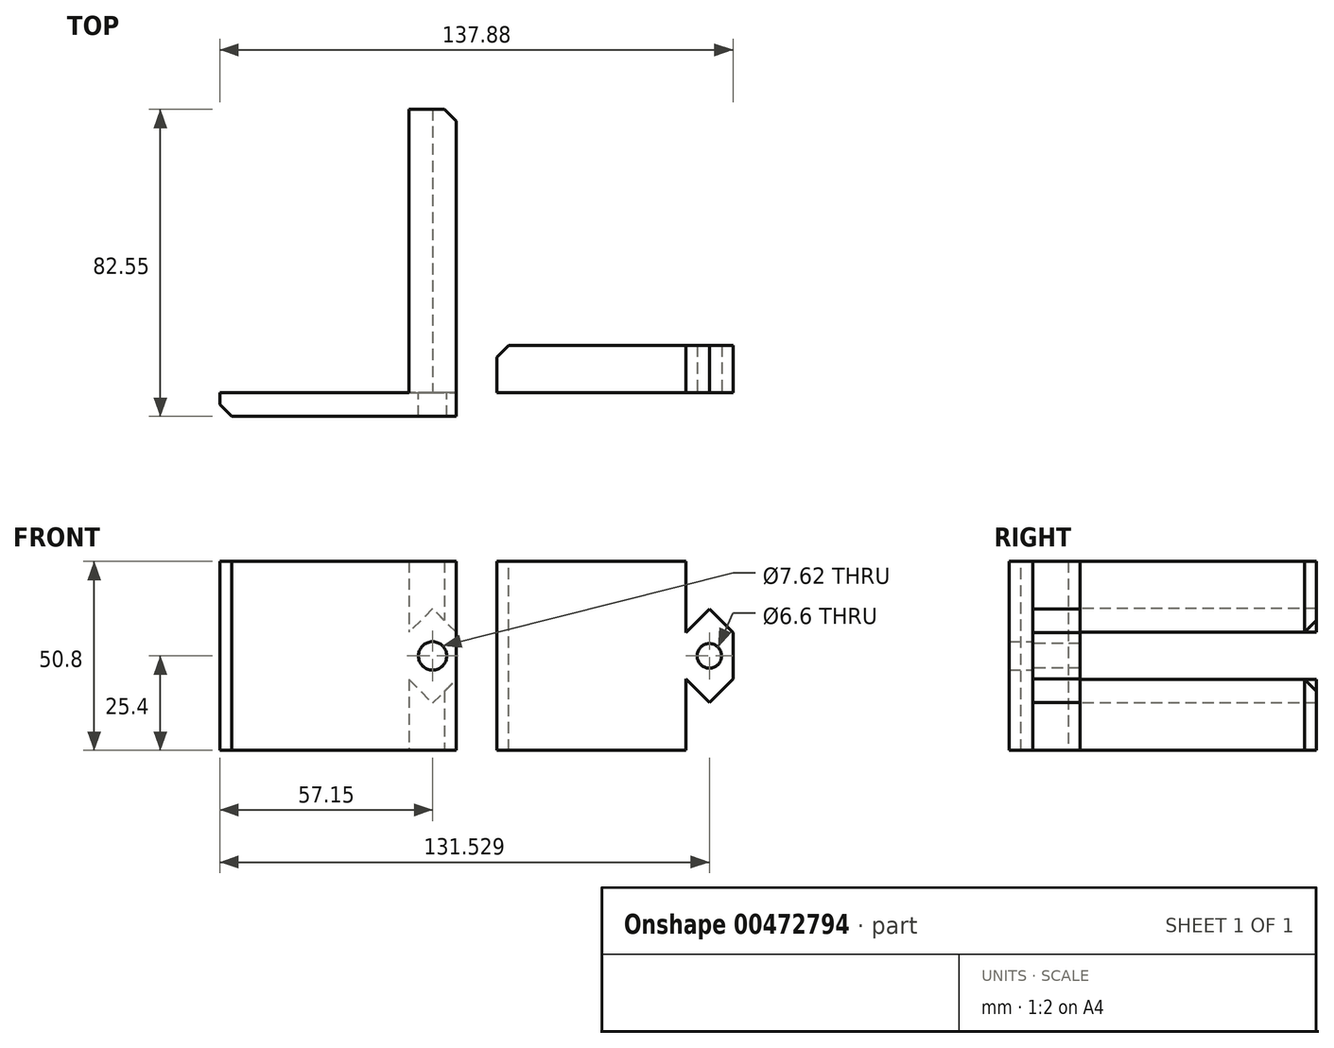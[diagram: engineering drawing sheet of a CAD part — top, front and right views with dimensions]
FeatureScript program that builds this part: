
annotation { "Feature Type Name" : "Feature", "Feature Type Description" : "" }
export const myFeature = defineFeature(function(context is Context, id is Id, definition is map)
    precondition{}
    {
        {
            var Q0;
            Q0=qCreatedBy(makeId("Top.planeOp"),FACE);
            var sketch = newSketch(context, id + "F0", { "sketchPlane" : qUnion([Q0])});
            skLineSegment(sketch, "E0", {"start": v(0, 0) * mm, "end": v(-50.8, 0) * mm});
            skLineSegment(sketch, "E1", {"start": v(0, 0) * mm, "end": v(0, 76.2) * mm});
            skLineSegment(sketch, "E2", {"start": v(0, 76.2) * mm, "end": v(12.7, 76.2) * mm});
            skLineSegment(sketch, "E3", {"start": v(12.7, 76.2) * mm, "end": v(12.7, -6.35) * mm});
            skLineSegment(sketch, "E4", {"start": v(12.7, -6.35) * mm, "end": v(-50.8, -6.35) * mm});
            skLineSegment(sketch, "E5", {"start": v(-50.8, -6.35) * mm, "end": v(-50.8, 0) * mm});
            skSolve(sketch);
        }
        {
            var Q0;
            Q0 = qSketchRegion(id + "F0", true);
            extrude(context, id + "F1", {"entities" : qUnion([Q0]), "depth" : 50.8 * mm});
        }
        {
            var Q0;
            Q0=makeQuery(id+"F1.opExtrude","SWEPT_EDGE",EDGE,{"disambiguationData":[OSD([sQuery(id+"F0.wireOp",EDGE,"E4"),sQuery(id+"F0.wireOp",EDGE,"E5")])]});
            var Q1;
            Q1=makeQuery(id+"F1.opExtrude","SWEPT_EDGE",EDGE,{"disambiguationData":[OSD([sQuery(id+"F0.wireOp",EDGE,"E2"),sQuery(id+"F0.wireOp",EDGE,"E3")])]});
            chamfer(context, id + "F2", {"entities" : qUnion([Q0, Q1]), "width" : 3.17 * mm, "tangentPropagation" : true});
        }
        {
            var Q0;
            Q0=qCreatedBy(makeId("Front.planeOp"),FACE);
            var sketch = newSketch(context, id + "F3", { "sketchPlane" : qUnion([Q0])});
            skLineSegment(sketch, "E6", {"start": v(0, 19.05) * mm, "end": v(6.35, 12.7) * mm});
            skLineSegment(sketch, "E7", {"start": v(6.35, 12.7) * mm, "end": v(12.7, 19.05) * mm});
            skLineSegment(sketch, "E8", {"start": v(12.7, 19.05) * mm, "end": v(12.7, 31.75) * mm});
            skLineSegment(sketch, "E9", {"start": v(0, 31.75) * mm, "end": v(0, 19.05) * mm});
            skLineSegment(sketch, "E10", {"start": v(12.7, 31.75) * mm, "end": v(6.4, 38.1) * mm});
            skLineSegment(sketch, "E11", {"start": v(6.4, 38.1) * mm, "end": v(0, 31.75) * mm});
            skSolve(sketch);
        }
        {
            var Q0;
            Q0 = qSketchRegion(id + "F3", true);
            extrude(context, id + "F4", {"entities" : qUnion([Q0]), "operationType" : NewBodyOperationType.REMOVE, "oppositeDirection" : true, "depth" : 76.2 * mm});
        }
        {
            var Q0;
            Q0=qCreatedBy(makeId("Front.planeOp"),FACE);
            var sketch = newSketch(context, id + "F5", { "sketchPlane" : qUnion([Q0])});
            skCircle(sketch, "E12", {"center": v(6.35, 25.4) * mm, "radius": 3.81 * mm});
            skSolve(sketch);
        }
        {
            var Q0;
            Q0 = qSketchRegion(id + "F5", true);
            extrude(context, id + "F6", {"entities" : qUnion([Q0]), "operationType" : NewBodyOperationType.REMOVE, "depth" : 25.88 * mm});
        }
        {
            var Q0;
            Q0=qCreatedBy(makeId("Front.planeOp"),FACE);
            var sketch = newSketch(context, id + "F7", { "sketchPlane" : qUnion([Q0])});
            skLineSegment(sketch, "E13", {"start": v(74.38, 31.62) * mm, "end": v(80.73, 37.97) * mm});
            skLineSegment(sketch, "E14", {"start": v(80.73, 37.97) * mm, "end": v(87.08, 31.62) * mm});
            skLineSegment(sketch, "E15", {"start": v(87.08, 31.62) * mm, "end": v(87.08, 19.18) * mm});
            skLineSegment(sketch, "E16", {"start": v(87.08, 19.18) * mm, "end": v(80.73, 12.83) * mm});
            skLineSegment(sketch, "E17", {"start": v(80.73, 12.83) * mm, "end": v(74.38, 19.18) * mm});
            skLineSegment(sketch, "E18", {"start": v(74.38, 19.18) * mm, "end": v(74.38, 0) * mm});
            skLineSegment(sketch, "E19", {"start": v(74.38, 0) * mm, "end": v(23.58, 0) * mm});
            skLineSegment(sketch, "E20", {"start": v(23.58, 0) * mm, "end": v(23.58, 50.8) * mm});
            skLineSegment(sketch, "E21", {"start": v(23.58, 50.8) * mm, "end": v(74.38, 50.8) * mm});
            skLineSegment(sketch, "E22", {"start": v(74.38, 50.8) * mm, "end": v(74.38, 31.62) * mm});
            skSolve(sketch);
        }
        {
            var Q0;
            Q0 = qSketchRegion(id + "F7", true);
            extrude(context, id + "F8", {"entities" : qUnion([Q0]), "depth" : 12.7 * mm});
        }
        {
            var Q0;
            Q0=qCreatedBy(makeId("Front.planeOp"),FACE);
            var sketch = newSketch(context, id + "F9", { "sketchPlane" : qUnion([Q0])});
            skCircle(sketch, "E23", {"center": v(80.73, 25.4) * mm, "radius": 3.3 * mm});
            skSolve(sketch);
        }
        {
            var Q0;
            Q0 = qSketchRegion(id + "F9", true);
            extrude(context, id + "F10", {"entities" : qUnion([Q0]), "operationType" : NewBodyOperationType.REMOVE, "depth" : 15 * mm});
        }
        {
            var Q0;
            Q0=makeQuery(id+"F8.opExtrude","CAP_EDGE",EDGE,{"disambiguationData":[OSD([sQuery(id+"F7.wireOp",EDGE,"E20")])],"isStart":false});
            chamfer(context, id + "F11", {"entities" : qUnion([Q0]), "width" : 3.17 * mm, "tangentPropagation" : true});
        }
        {
            var Q0;
            Q0=makeQuery(id+"F8.opExtrude","SWEPT_BODY",BODY,{"disambiguationData":[OSD([sQuery(id+"F7.wireOp",EDGE,"E13"),sQuery(id+"F7.wireOp",EDGE,"E14"),sQuery(id+"F7.wireOp",EDGE,"E15"),sQuery(id+"F7.wireOp",EDGE,"E16"),sQuery(id+"F7.wireOp",EDGE,"E17"),sQuery(id+"F7.wireOp",EDGE,"E18"),sQuery(id+"F7.wireOp",EDGE,"E19"),sQuery(id+"F7.wireOp",EDGE,"E20"),sQuery(id+"F7.wireOp",EDGE,"E21"),sQuery(id+"F7.wireOp",EDGE,"E22")])]});
            var Q1;
            Q1=makeQuery(id+"F8.opExtrude","CAP_EDGE",EDGE,{"disambiguationData":[OSD([sQuery(id+"F7.wireOp",EDGE,"E19")])],"isStart":false});
            var Q2;
            Q2=makeQuery(id+"F8.opExtrude","CAP_EDGE",EDGE,{"disambiguationData":[OSD([sQuery(id+"F7.wireOp",EDGE,"E19")])],"isStart":true});
            transform(context, id + "F12", {"entities" : qUnion([Q0]), "transformType" : TransformType.ROTATION, "transformAxis" : qUnion([Q2]), "angle" : 180 * degree, "makeCopy" : false});
        }
        {
            var Q0;
            Q0=makeQuery(id+"F8.opExtrude","SWEPT_BODY",BODY,{"disambiguationData":[OSD([sQuery(id+"F7.wireOp",EDGE,"E13"),sQuery(id+"F7.wireOp",EDGE,"E14"),sQuery(id+"F7.wireOp",EDGE,"E15"),sQuery(id+"F7.wireOp",EDGE,"E16"),sQuery(id+"F7.wireOp",EDGE,"E17"),sQuery(id+"F7.wireOp",EDGE,"E18"),sQuery(id+"F7.wireOp",EDGE,"E19"),sQuery(id+"F7.wireOp",EDGE,"E20"),sQuery(id+"F7.wireOp",EDGE,"E21"),sQuery(id+"F7.wireOp",EDGE,"E22")])]});
            var Q1;
            Q1=makeQuery(id+"F8.opExtrude","CAP_EDGE",EDGE,{"disambiguationData":[OSD([sQuery(id+"F7.wireOp",EDGE,"E20")])],"isStart":true});
            transform(context, id + "F13", {"entities" : qUnion([Q0]), "transformType" : TransformType.TRANSLATION_ENTITY, "oppositeDirectionEntity" : true, "transformLine" : qUnion([Q1]), "makeCopy" : false});
        }
    });
